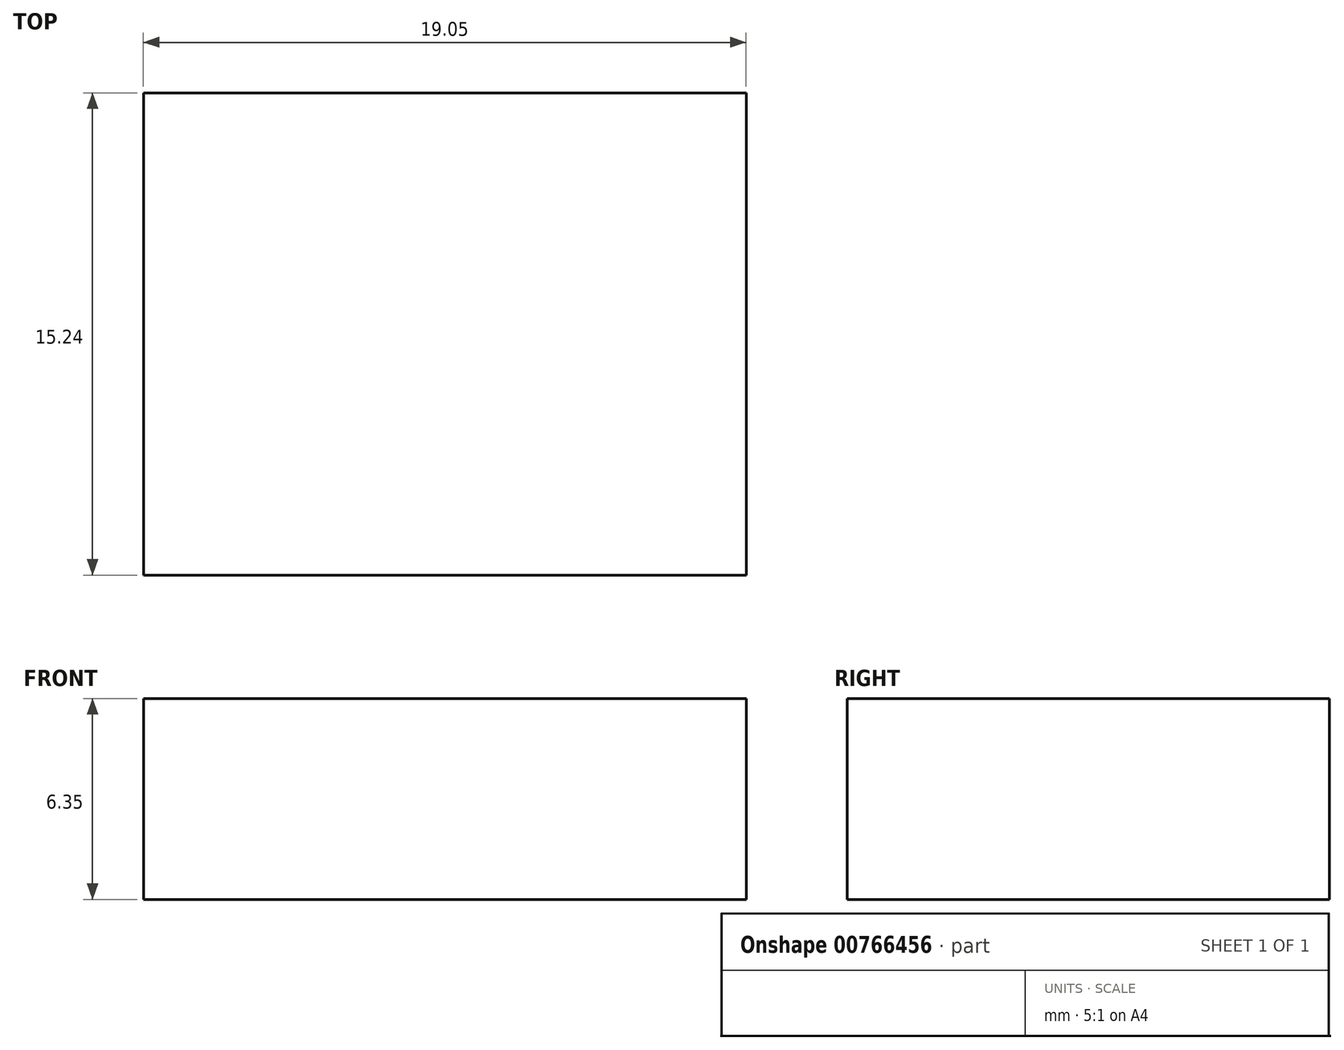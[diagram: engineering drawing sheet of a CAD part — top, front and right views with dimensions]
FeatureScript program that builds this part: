
annotation { "Feature Type Name" : "Feature", "Feature Type Description" : "" }
export const myFeature = defineFeature(function(context is Context, id is Id, definition is map)
    precondition{}
    {
        {
            var Q0;
            Q0=qCreatedBy(makeId("Top.planeOp"),FACE);
            var sketch = newSketch(context, id + "F0", { "sketchPlane" : qUnion([Q0])});
            skLineSegment(sketch, "E0.bottom", {"start": v(15.6, 7.78) * mm, "end": v(34.65, 7.78) * mm});
            skLineSegment(sketch, "E0.top", {"start": v(15.6, -7.46) * mm, "end": v(34.65, -7.46) * mm});
            skLineSegment(sketch, "E0.left", {"start": v(15.6, 7.78) * mm, "end": v(15.6, -7.46) * mm});
            skLineSegment(sketch, "E0.right", {"start": v(34.65, 7.78) * mm, "end": v(34.65, -7.46) * mm});
            skSolve(sketch);
        }
        {
            var Q0;
            Q0=makeQuery(id+"F0.imprint","IMPRINT",FACE,{"disambiguationData":[TD([[makeQuery(id+"F0.imprint","IMPRINT",EDGE,{"derivedFrom":sQuery(id+"F0.wireOp",EDGE,"E0.bottom")}),-1.0]])]});
            extrude(context, id + "F1", {"entities" : qUnion([Q0]), "depth" : 6.35 * mm, "offsetDistance" : 25.4 * mm});
        }
    });
